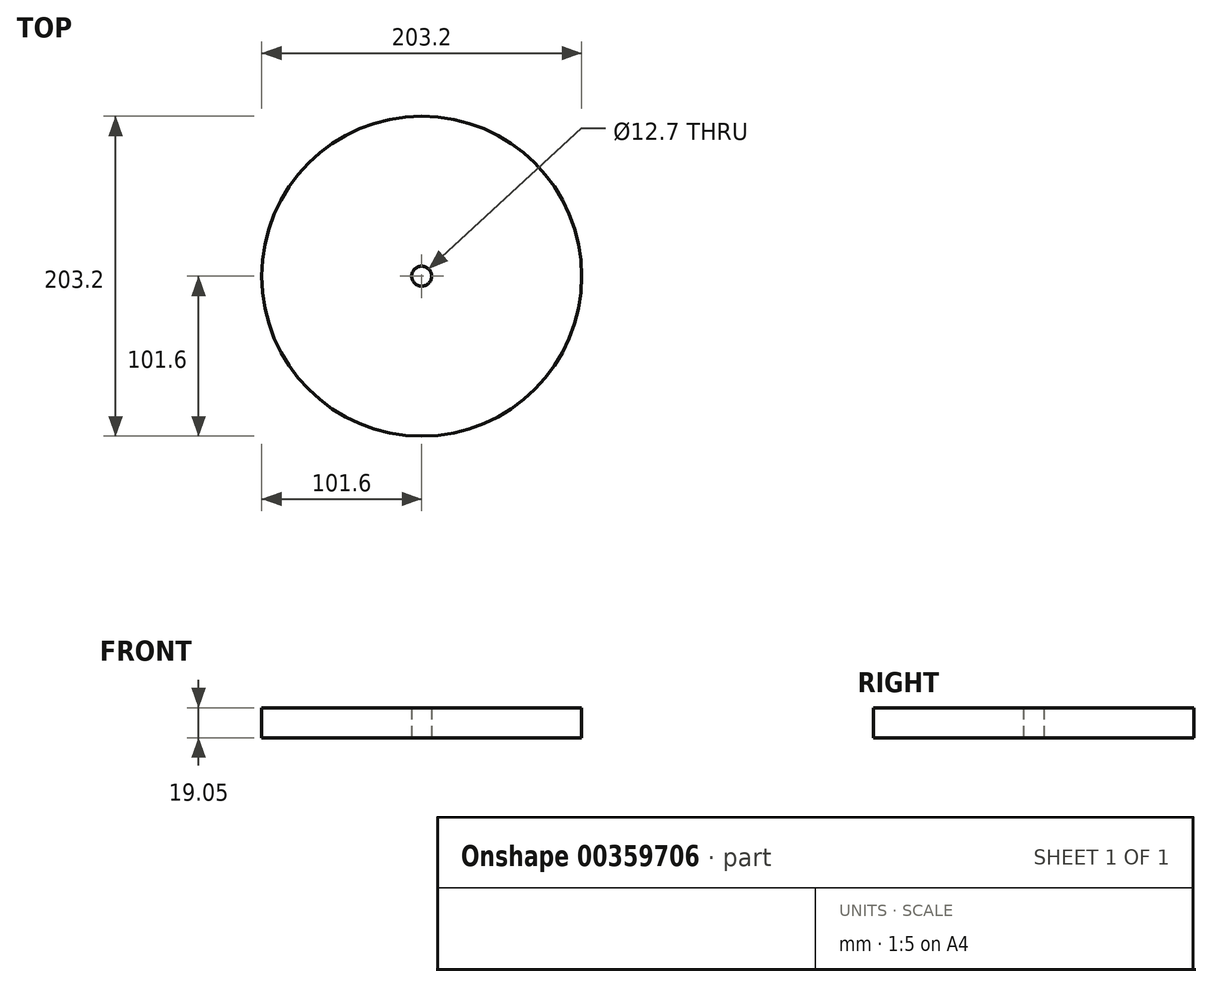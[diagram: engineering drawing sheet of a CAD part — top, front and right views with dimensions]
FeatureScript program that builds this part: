
annotation { "Feature Type Name" : "Feature", "Feature Type Description" : "" }
export const myFeature = defineFeature(function(context is Context, id is Id, definition is map)
    precondition{}
    {
        {
            var Q0;
            Q0=qCreatedBy(makeId("Top.planeOp"),FACE);
            var sketch = newSketch(context, id + "F0", { "sketchPlane" : qUnion([Q0])});
            skCircle(sketch, "E0", {"center": v(0, 0) * mm, "radius": 101.6 * mm});
            skCircle(sketch, "E1", {"center": v(0, 0) * mm, "radius": 6.35 * mm});
            skSolve(sketch);
        }
        {
            var Q0;
            Q0 = qSketchRegion(id + "F0", true);
            extrude(context, id + "F1", {"entities" : qUnion([Q0]), "depth" : 19.05 * mm});
        }
    });
